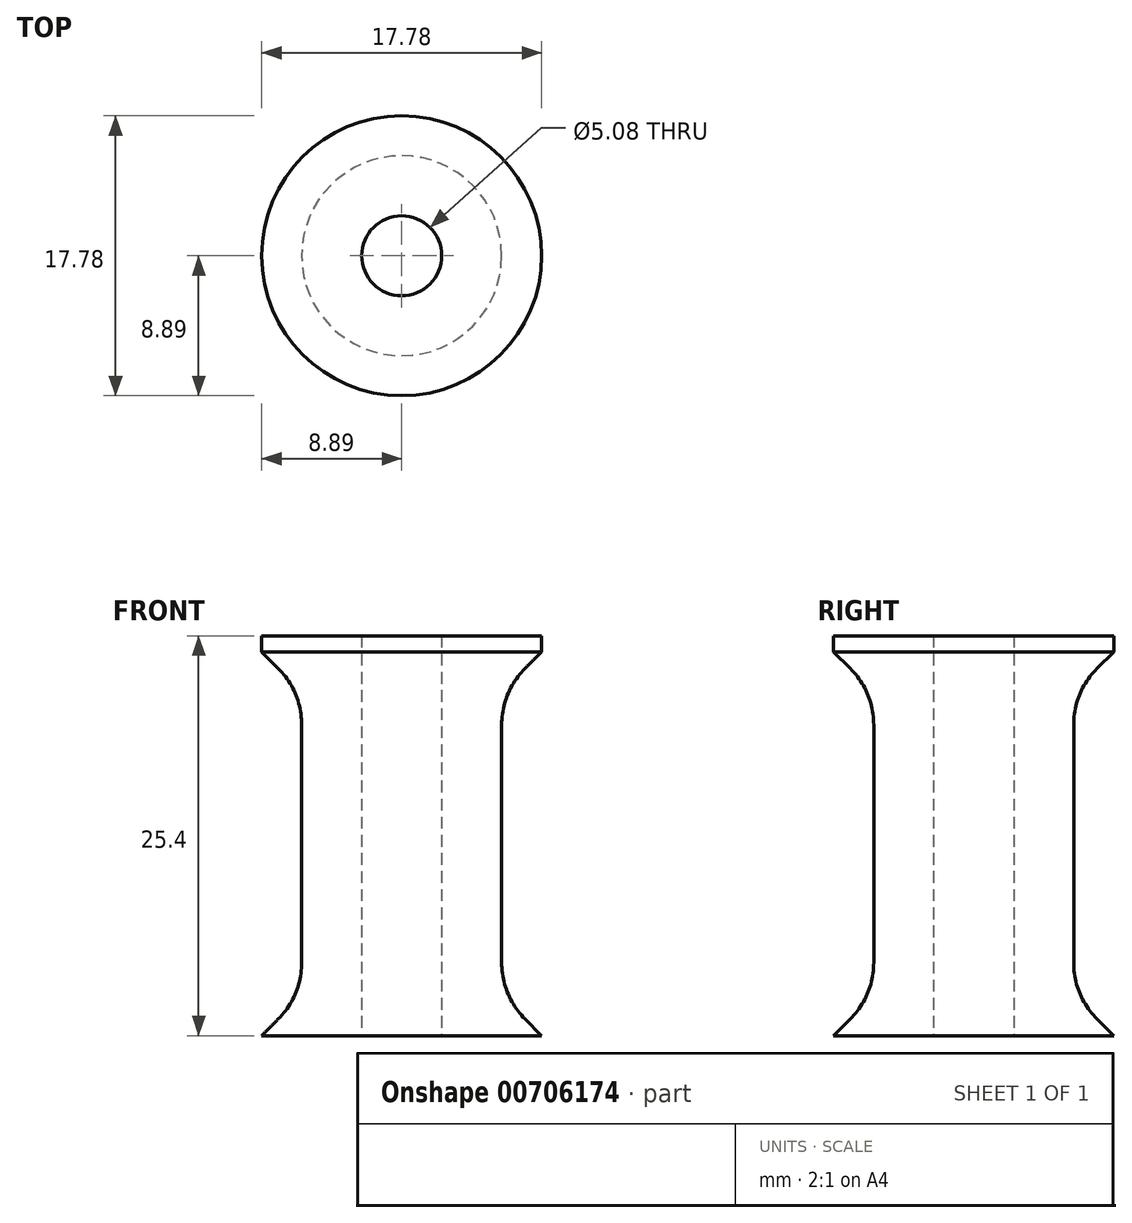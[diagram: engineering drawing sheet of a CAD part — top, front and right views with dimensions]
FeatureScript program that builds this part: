
annotation { "Feature Type Name" : "Feature", "Feature Type Description" : "" }
export const myFeature = defineFeature(function(context is Context, id is Id, definition is map)
    precondition{}
    {
        {
            var Q0;
            Q0=qCreatedBy(makeId("Front.planeOp"),FACE);
            var sketch = newSketch(context, id + "F0", { "sketchPlane" : qUnion([Q0])});
            skLineSegment(sketch, "E0", {"start": v(0, 0) * mm, "end": v(0, 37.33) * mm, "construction": true});
            skLineSegment(sketch, "E1", {"start": v(0, 0) * mm, "end": v(2.54, 0) * mm, "construction": true});
            skLineSegment(sketch, "E2", {"start": v(2.54, 0) * mm, "end": v(2.54, 25.4) * mm});
            skLineSegment(sketch, "E3", {"start": v(2.54, 25.4) * mm, "end": v(0, 25.4) * mm, "construction": true});
            skLineSegment(sketch, "E4", {"start": v(2.54, 0) * mm, "end": v(8.9, 0) * mm});
            skLineSegment(sketch, "E5", {"start": v(2.54, 25.4) * mm, "end": v(8.89, 25.4) * mm});
            skLineSegment(sketch, "E6", {"start": v(6.35, 21.84) * mm, "end": v(6.35, 2.54) * mm});
            skLineSegment(sketch, "E7", {"start": v(6.35, 2.54) * mm, "end": v(8.9, 0) * mm});
            skLineSegment(sketch, "E8", {"start": v(8.89, 25.4) * mm, "end": v(8.89, 24.38) * mm});
            skLineSegment(sketch, "E9", {"start": v(8.89, 24.38) * mm, "end": v(6.35, 21.84) * mm});
            skSolve(sketch);
        }
        {
            var Q0;
            Q0=makeQuery(id+"F0.imprint","IMPRINT",FACE,{"disambiguationData":[TD([[makeQuery(id+"F0.imprint","IMPRINT",EDGE,{"derivedFrom":sQuery(id+"F0.wireOp",EDGE,"E2")}),-1.0]])]});
            var Q1;
            Q1=sQuery(id+"F0.wireOp",EDGE,"E0");
            revolve(context, id + "F1", {"surfaceOperationType" : NewSurfaceOperationType.NEW, "entities" : qUnion([Q0]), "axis" : qUnion([Q1]), "revolveType" : RevolveType.FULL});
        }
        {
            var Q0;
            Q0=makeQuery(id+"F1.opRevolve","SWEPT_EDGE",EDGE,{"disambiguationData":[OSD([sQuery(id+"F0.wireOp",EDGE,"E6"),sQuery(id+"F0.wireOp",EDGE,"E9")])]});
            var Q1;
            Q1=makeQuery(id+"F1.opRevolve","SWEPT_EDGE",EDGE,{"disambiguationData":[OSD([sQuery(id+"F0.wireOp",EDGE,"E6"),sQuery(id+"F0.wireOp",EDGE,"E7")])]});
            fillet(context, id + "F2", {"entities" : qUnion([Q0, Q1]), "radius" : 5.08 * mm, "tangentPropagation" : true, "allowEdgeOverflow" : false});
        }
    });
